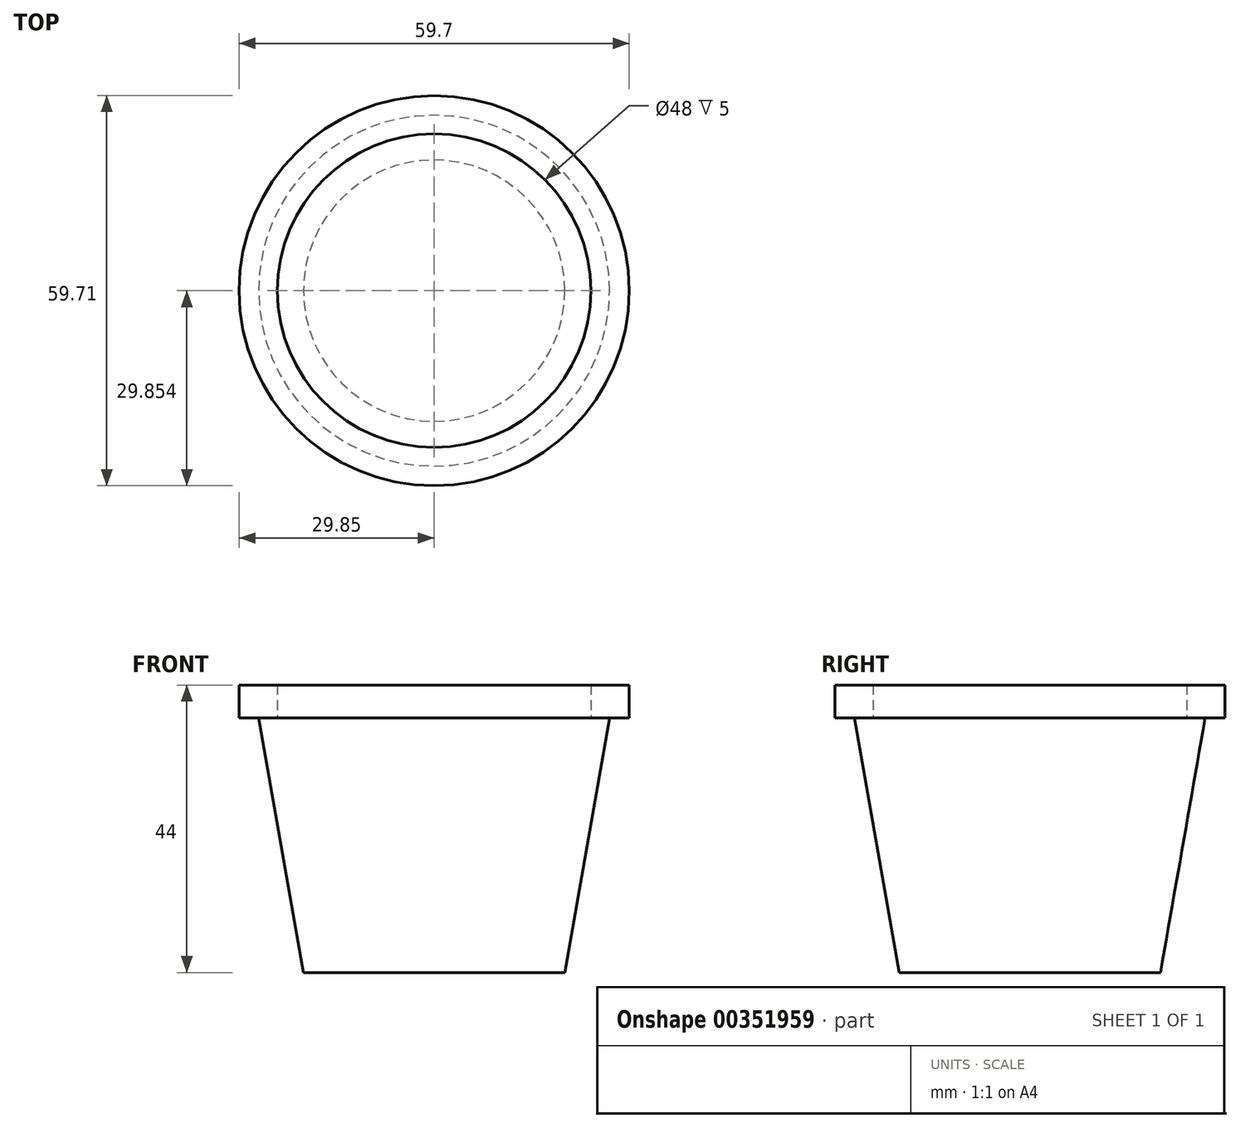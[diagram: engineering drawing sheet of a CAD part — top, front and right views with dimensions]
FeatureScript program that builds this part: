
annotation { "Feature Type Name" : "Feature", "Feature Type Description" : "" }
export const myFeature = defineFeature(function(context is Context, id is Id, definition is map)
    precondition{}
    {
        {
            var Q0;
            Q0=qCreatedBy(makeId("Right.planeOp"),FACE);
            var sketch = newSketch(context, id + "F0", { "sketchPlane" : qUnion([Q0])});
            skLineSegment(sketch, "E0", {"start": v(-15.98, -0.3) * mm, "end": v(4.02, -0.3) * mm});
            skLineSegment(sketch, "E1", {"start": v(4.02, -0.3) * mm, "end": v(4.02, 38.7) * mm});
            skLineSegment(sketch, "E2", {"start": v(4.02, 38.7) * mm, "end": v(-19.98, 38.7) * mm});
            skLineSegment(sketch, "E3", {"start": v(-19.98, 38.7) * mm, "end": v(-19.98, 43.7) * mm});
            skLineSegment(sketch, "E4", {"start": v(-15.98, -0.3) * mm, "end": v(-22.83, 38.7) * mm});
            skLineSegment(sketch, "E5", {"start": v(-22.83, 38.7) * mm, "end": v(-25.83, 38.7) * mm});
            skLineSegment(sketch, "E6", {"start": v(-25.83, 38.7) * mm, "end": v(-25.83, 43.7) * mm});
            skLineSegment(sketch, "E7", {"start": v(-25.83, 43.7) * mm, "end": v(-19.98, 43.7) * mm});
            skSolve(sketch);
        }
        {
            var Q0;
            Q0=makeQuery(id+"F0.imprint","IMPRINT",FACE,{"disambiguationData":[TD([[makeQuery(id+"F0.imprint","IMPRINT",EDGE,{"derivedFrom":sQuery(id+"F0.wireOp",EDGE,"E0")}),1.0]])]});
            var Q1;
            Q1=sQuery(id+"F0.wireOp",EDGE,"E1");
            revolve(context, id + "F1", {"entities" : qUnion([Q0]), "axis" : qUnion([Q1]), "revolveType" : RevolveType.FULL});
        }
    });
